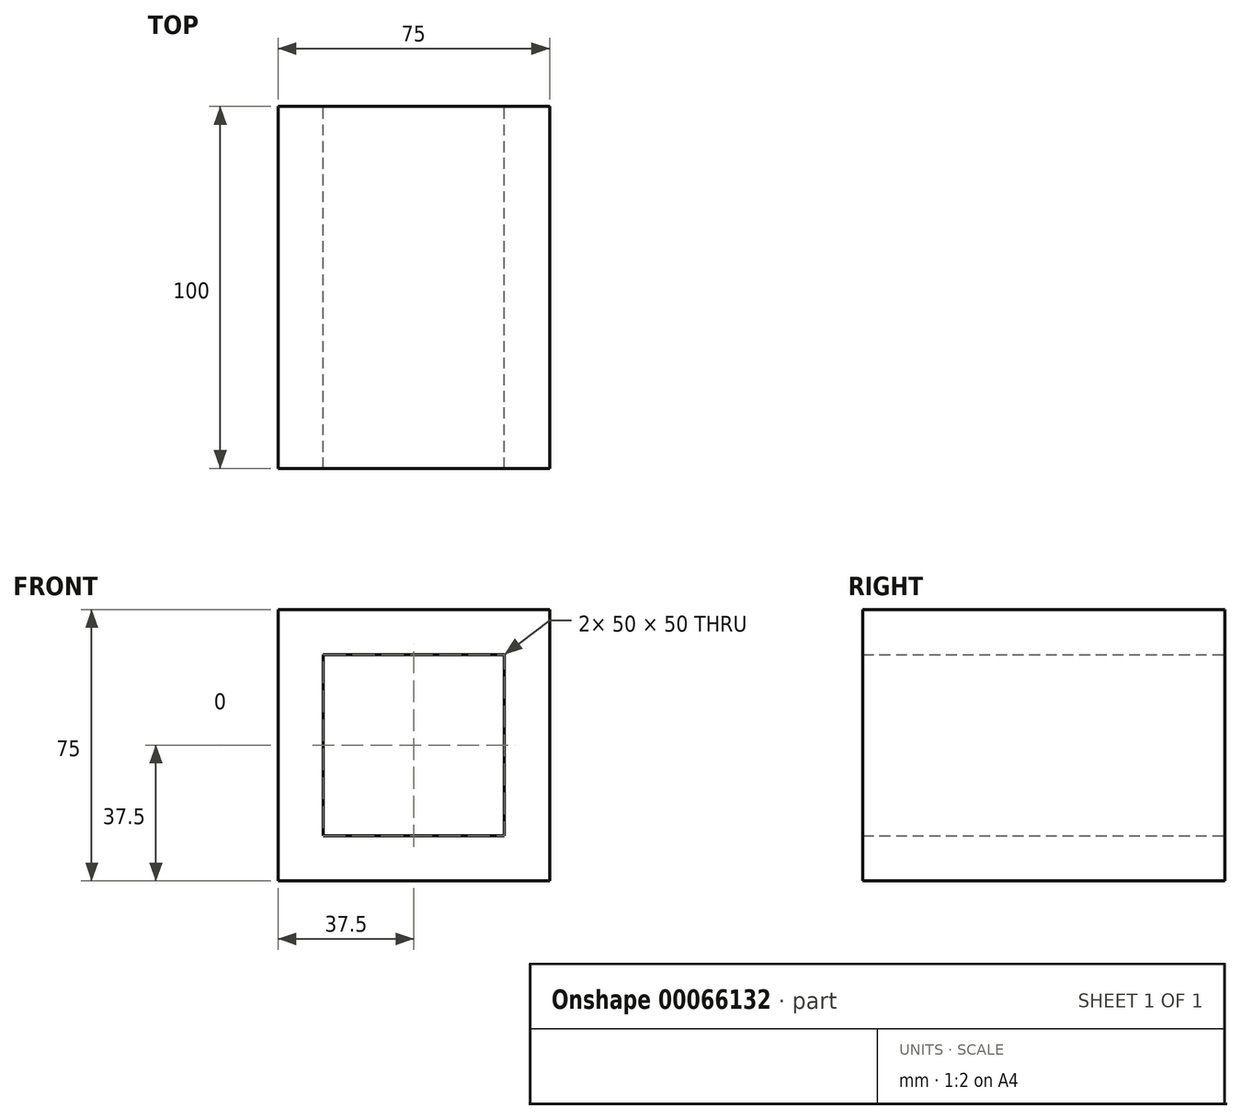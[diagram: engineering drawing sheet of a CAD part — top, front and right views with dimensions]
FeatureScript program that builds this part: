
annotation { "Feature Type Name" : "Feature", "Feature Type Description" : "" }
export const myFeature = defineFeature(function(context is Context, id is Id, definition is map)
    precondition{}
    {
        {
            var Q0;
            Q0=qCreatedBy(makeId("Front.planeOp"),FACE);
            var sketch = newSketch(context, id + "F0", { "sketchPlane" : qUnion([Q0])});
            skLineSegment(sketch, "E0.rect.bottom", {"start": v(25, -25) * mm, "end": v(-25, -25) * mm});
            skLineSegment(sketch, "E0.rect.top", {"start": v(25, 25) * mm, "end": v(-25, 25) * mm});
            skLineSegment(sketch, "E0.rect.left", {"start": v(25, -25) * mm, "end": v(25, 25) * mm});
            skLineSegment(sketch, "E0.rect.right", {"start": v(-25, -25) * mm, "end": v(-25, 25) * mm});
            skPoint(sketch, "E0.rect.middle", {"position": v(0, 0) * mm});
            skLineSegment(sketch, "E1.rect.bottom", {"start": v(37.5, -37.5) * mm, "end": v(-37.5, -37.5) * mm});
            skLineSegment(sketch, "E1.rect.top", {"start": v(37.5, 37.5) * mm, "end": v(-37.5, 37.5) * mm});
            skLineSegment(sketch, "E1.rect.left", {"start": v(37.5, -37.5) * mm, "end": v(37.5, 37.5) * mm});
            skLineSegment(sketch, "E1.rect.right", {"start": v(-37.5, -37.5) * mm, "end": v(-37.5, 37.5) * mm});
            skSolve(sketch);
        }
        {
            var Q0;
            Q0 = qSketchRegion(id + "F0", true);
            extrude(context, id + "F1", {"entities" : qUnion([Q0]), "depth" : 100 * mm});
        }
    });
